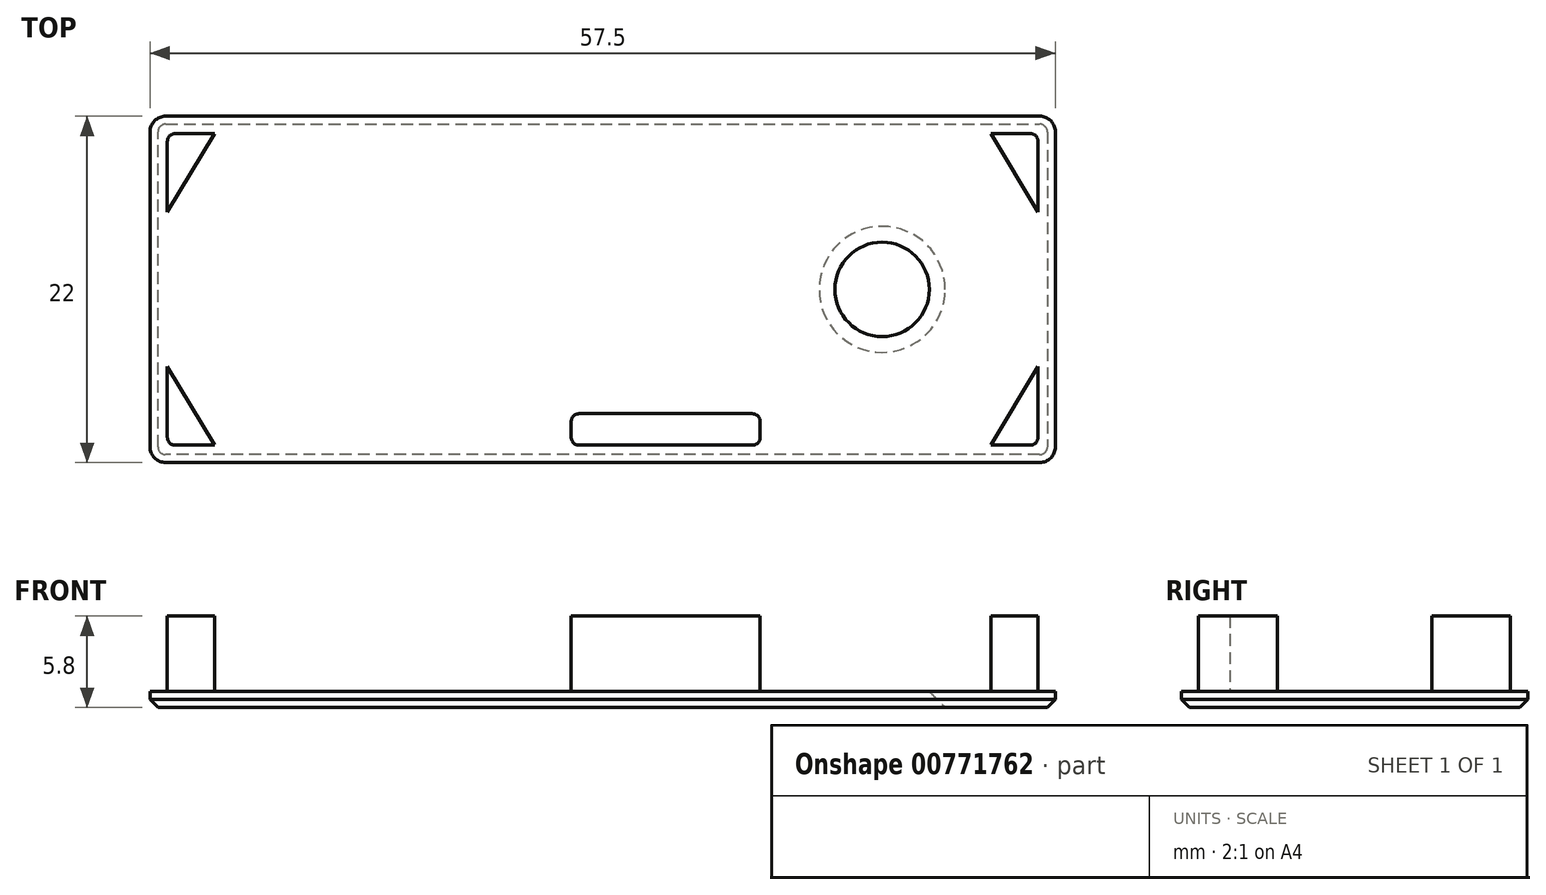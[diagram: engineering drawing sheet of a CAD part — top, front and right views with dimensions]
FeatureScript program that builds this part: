
annotation { "Feature Type Name" : "Feature", "Feature Type Description" : "" }
export const myFeature = defineFeature(function(context is Context, id is Id, definition is map)
    precondition{}
    {
        {
            var Q0;
            Q0=qCreatedBy(makeId("Top.planeOp"),FACE);
            var sketch = newSketch(context, id + "F0", { "sketchPlane" : qUnion([Q0])});
            skLineSegment(sketch, "E0.bottom", {"start": v(1, 22) * mm, "end": v(56.5, 22) * mm});
            skLineSegment(sketch, "E0.top", {"start": v(1, 0) * mm, "end": v(56.5, 0) * mm});
            skLineSegment(sketch, "E0.left", {"start": v(0, 21) * mm, "end": v(0, 1) * mm});
            skLineSegment(sketch, "E0.right", {"start": v(57.5, 21) * mm, "end": v(57.5, 1) * mm});
            skPoint(sketch, "E1.visualSharp", {"position": v(0, 22) * mm});
            skArc(sketch, "E1.filletArc", {"start": v(1, 22) * mm, "mid": v(0.3, 21.7) * mm, "end": v(0, 21) * mm});
            skPoint(sketch, "E2.visualSharp", {"position": v(0, 0) * mm});
            skArc(sketch, "E2.filletArc", {"start": v(0, 1) * mm, "mid": v(0.3, 0.3) * mm, "end": v(1, 0) * mm});
            skPoint(sketch, "E3.visualSharp", {"position": v(57.5, 0) * mm});
            skArc(sketch, "E3.filletArc", {"start": v(56.5, 0) * mm, "mid": v(57.2, 0.3) * mm, "end": v(57.5, 1) * mm});
            skPoint(sketch, "E4.visualSharp", {"position": v(57.5, 22) * mm});
            skArc(sketch, "E4.filletArc", {"start": v(57.5, 21) * mm, "mid": v(57.2, 21.7) * mm, "end": v(56.5, 22) * mm});
            skLineSegment(sketch, "E5", {"start": v(28.17, 11) * mm, "end": v(66.86, 11) * mm, "construction": true});
            skLineSegment(sketch, "E6", {"start": v(46.5, 24.71) * mm, "end": v(46.5, -8.57) * mm, "construction": true});
            skLineSegment(sketch, "E7.0", {"start": v(1, 21) * mm, "end": v(56.5, 21) * mm, "construction": true});
            skLineSegment(sketch, "E7.1", {"start": v(1, 21) * mm, "end": v(1, 1) * mm, "construction": true});
            skLineSegment(sketch, "E7.2", {"start": v(1, 1) * mm, "end": v(56.5, 1) * mm, "construction": true});
            skLineSegment(sketch, "E7.3", {"start": v(56.5, 21) * mm, "end": v(56.5, 1) * mm, "construction": true});
            skCircle(sketch, "E8", {"center": v(46.5, 11) * mm, "radius": 3 * mm});
            skSolve(sketch);
        }
        {
            var Q0;
            Q0 = qSketchRegion(id + "F0", true);
            extrude(context, id + "F1", {"entities" : qUnion([Q0]), "depth" : 1 * mm, "offsetDistance" : 25 * mm});
        }
        {
            var Q0;
            Q0=makeQuery(id+"F1.opExtrude","CAP_FACE",FACE,{"disambiguationData":[OSD([sQuery(id+"F0.wireOp",EDGE,"E0.bottom"),sQuery(id+"F0.wireOp",EDGE,"E0.top"),sQuery(id+"F0.wireOp",EDGE,"E0.left"),sQuery(id+"F0.wireOp",EDGE,"E0.right"),sQuery(id+"F0.wireOp",EDGE,"E1.filletArc"),sQuery(id+"F0.wireOp",EDGE,"E2.filletArc"),sQuery(id+"F0.wireOp",EDGE,"E3.filletArc"),sQuery(id+"F0.wireOp",EDGE,"E4.filletArc"),sQuery(id+"F0.wireOp",EDGE,"E8")])],"isStart":false});
            var sketch = newSketch(context, id + "F2", { "sketchPlane" : qUnion([Q0])});
            skLineSegment(sketch, "E9", {"start": v(28.75, 21) * mm, "end": v(28.75, 1) * mm, "construction": true});
            skLineSegment(sketch, "E10", {"start": v(1.1, 15.9) * mm, "end": v(1.1, 20.4) * mm});
            skLineSegment(sketch, "E11", {"start": v(1.6, 20.9) * mm, "end": v(4.1, 20.9) * mm});
            skLineSegment(sketch, "E12", {"start": v(4.1, 20.9) * mm, "end": v(1.1, 15.9) * mm});
            skPoint(sketch, "E13.visualSharp", {"position": v(1.1, 20.9) * mm});
            skArc(sketch, "E13.filletArc", {"start": v(1.6, 20.9) * mm, "mid": v(1.25, 20.75) * mm, "end": v(1.1, 20.4) * mm});
            skArc(sketch, "E14.MirrorCS", {"start": v(55.9, 20.9) * mm, "mid": v(56.25, 20.75) * mm, "end": v(56.4, 20.4) * mm});
            skLineSegment(sketch, "E15.MirrorCS", {"start": v(55.9, 20.9) * mm, "end": v(53.4, 20.9) * mm});
            skLineSegment(sketch, "E16.MirrorCS", {"start": v(53.4, 20.9) * mm, "end": v(56.4, 15.9) * mm});
            skLineSegment(sketch, "E17.MirrorCS", {"start": v(56.4, 15.9) * mm, "end": v(56.4, 20.4) * mm});
            skPoint(sketch, "E18.MirrorP", {"position": v(56.4, 20.9) * mm});
            skArc(sketch, "E19.MirrorCS", {"start": v(1.6, 1.1) * mm, "mid": v(1.25, 1.25) * mm, "end": v(1.1, 1.6) * mm});
            skArc(sketch, "E20.MirrorCS", {"start": v(55.9, 1.1) * mm, "mid": v(56.25, 1.25) * mm, "end": v(56.4, 1.6) * mm});
            skLineSegment(sketch, "E21.MirrorCS", {"start": v(1.1, 6.1) * mm, "end": v(1.1, 1.6) * mm});
            skPoint(sketch, "E22.MirrorP", {"position": v(1.1, 1.1) * mm});
            skLineSegment(sketch, "E23.MirrorCS", {"start": v(55.9, 1.1) * mm, "end": v(53.4, 1.1) * mm});
            skLineSegment(sketch, "E24.MirrorCS", {"start": v(4.1, 1.1) * mm, "end": v(1.1, 6.1) * mm});
            skLineSegment(sketch, "E25.MirrorCS", {"start": v(53.4, 1.1) * mm, "end": v(56.4, 6.1) * mm});
            skLineSegment(sketch, "E26.MirrorCS", {"start": v(56.4, 6.1) * mm, "end": v(56.4, 1.6) * mm});
            skLineSegment(sketch, "E27.MirrorCS", {"start": v(1.6, 1.1) * mm, "end": v(4.1, 1.1) * mm});
            skPoint(sketch, "E28.MirrorP", {"position": v(56.4, 1.1) * mm});
            skLineSegment(sketch, "E29.bottom", {"start": v(27.25, 3.1) * mm, "end": v(38.25, 3.1) * mm});
            skLineSegment(sketch, "E29.top", {"start": v(27.25, 1.1) * mm, "end": v(38.25, 1.1) * mm});
            skLineSegment(sketch, "E29.left", {"start": v(26.75, 2.6) * mm, "end": v(26.75, 1.6) * mm});
            skLineSegment(sketch, "E29.right", {"start": v(38.75, 2.6) * mm, "end": v(38.75, 1.6) * mm});
            skPoint(sketch, "E30.visualSharp", {"position": v(26.75, 1.1) * mm});
            skArc(sketch, "E30.filletArc", {"start": v(26.75, 1.6) * mm, "mid": v(26.9, 1.25) * mm, "end": v(27.25, 1.1) * mm});
            skPoint(sketch, "E31.visualSharp", {"position": v(26.75, 3.1) * mm});
            skArc(sketch, "E31.filletArc", {"start": v(27.25, 3.1) * mm, "mid": v(26.9, 2.95) * mm, "end": v(26.75, 2.6) * mm});
            skPoint(sketch, "E32.visualSharp", {"position": v(38.75, 3.1) * mm});
            skArc(sketch, "E32.filletArc", {"start": v(38.75, 2.6) * mm, "mid": v(38.6, 2.95) * mm, "end": v(38.25, 3.1) * mm});
            skPoint(sketch, "E33.visualSharp", {"position": v(38.75, 1.1) * mm});
            skArc(sketch, "E33.filletArc", {"start": v(38.25, 1.1) * mm, "mid": v(38.6, 1.25) * mm, "end": v(38.75, 1.6) * mm});
            skSolve(sketch);
        }
        {
            var Q0;
            Q0 = qSketchRegion(id + "F2", true);
            extrude(context, id + "F3", {"entities" : qUnion([Q0]), "operationType" : NewBodyOperationType.ADD, "depth" : 4.8 * mm, "offsetDistance" : 25 * mm});
        }
        {
            var Q0;
            Q0=makeQuery(id+"F1.opExtrude","CAP_EDGE",EDGE,{"disambiguationData":[OSD([sQuery(id+"F0.wireOp",EDGE,"E8")])],"isStart":true});
            chamfer(context, id + "F4", {"entities" : qUnion([Q0]), "width" : 1 * mm, "tangentPropagation" : true});
        }
        {
            var Q0;
            Q0=makeQuery(id+"F1.opExtrude","CAP_EDGE",EDGE,{"disambiguationData":[OSD([sQuery(id+"F0.wireOp",EDGE,"E0.top")])],"isStart":true});
            var Q1;
            Q1=makeQuery(id+"F1.opExtrude","CAP_EDGE",EDGE,{"disambiguationData":[OSD([sQuery(id+"F0.wireOp",EDGE,"E0.left")])],"isStart":true});
            var Q2;
            Q2=makeQuery(id+"F1.opExtrude","CAP_EDGE",EDGE,{"disambiguationData":[OSD([sQuery(id+"F0.wireOp",EDGE,"E2.filletArc")])],"isStart":true});
            var Q3;
            Q3=makeQuery(id+"F1.opExtrude","CAP_EDGE",EDGE,{"disambiguationData":[OSD([sQuery(id+"F0.wireOp",EDGE,"E1.filletArc")])],"isStart":true});
            var Q4;
            Q4=makeQuery(id+"F1.opExtrude","CAP_EDGE",EDGE,{"disambiguationData":[OSD([sQuery(id+"F0.wireOp",EDGE,"E0.bottom")])],"isStart":true});
            var Q5;
            Q5=makeQuery(id+"F1.opExtrude","CAP_EDGE",EDGE,{"disambiguationData":[OSD([sQuery(id+"F0.wireOp",EDGE,"E0.right")])],"isStart":true});
            var Q6;
            Q6=makeQuery(id+"F1.opExtrude","CAP_EDGE",EDGE,{"disambiguationData":[OSD([sQuery(id+"F0.wireOp",EDGE,"E3.filletArc")])],"isStart":true});
            var Q7;
            Q7=makeQuery(id+"F1.opExtrude","CAP_EDGE",EDGE,{"disambiguationData":[OSD([sQuery(id+"F0.wireOp",EDGE,"E4.filletArc")])],"isStart":true});
            chamfer(context, id + "F5", {"entities" : qUnion([Q0, Q1, Q2, Q3, Q4, Q5, Q6, Q7]), "width" : .5 * mm, "tangentPropagation" : true});
        }
    });
